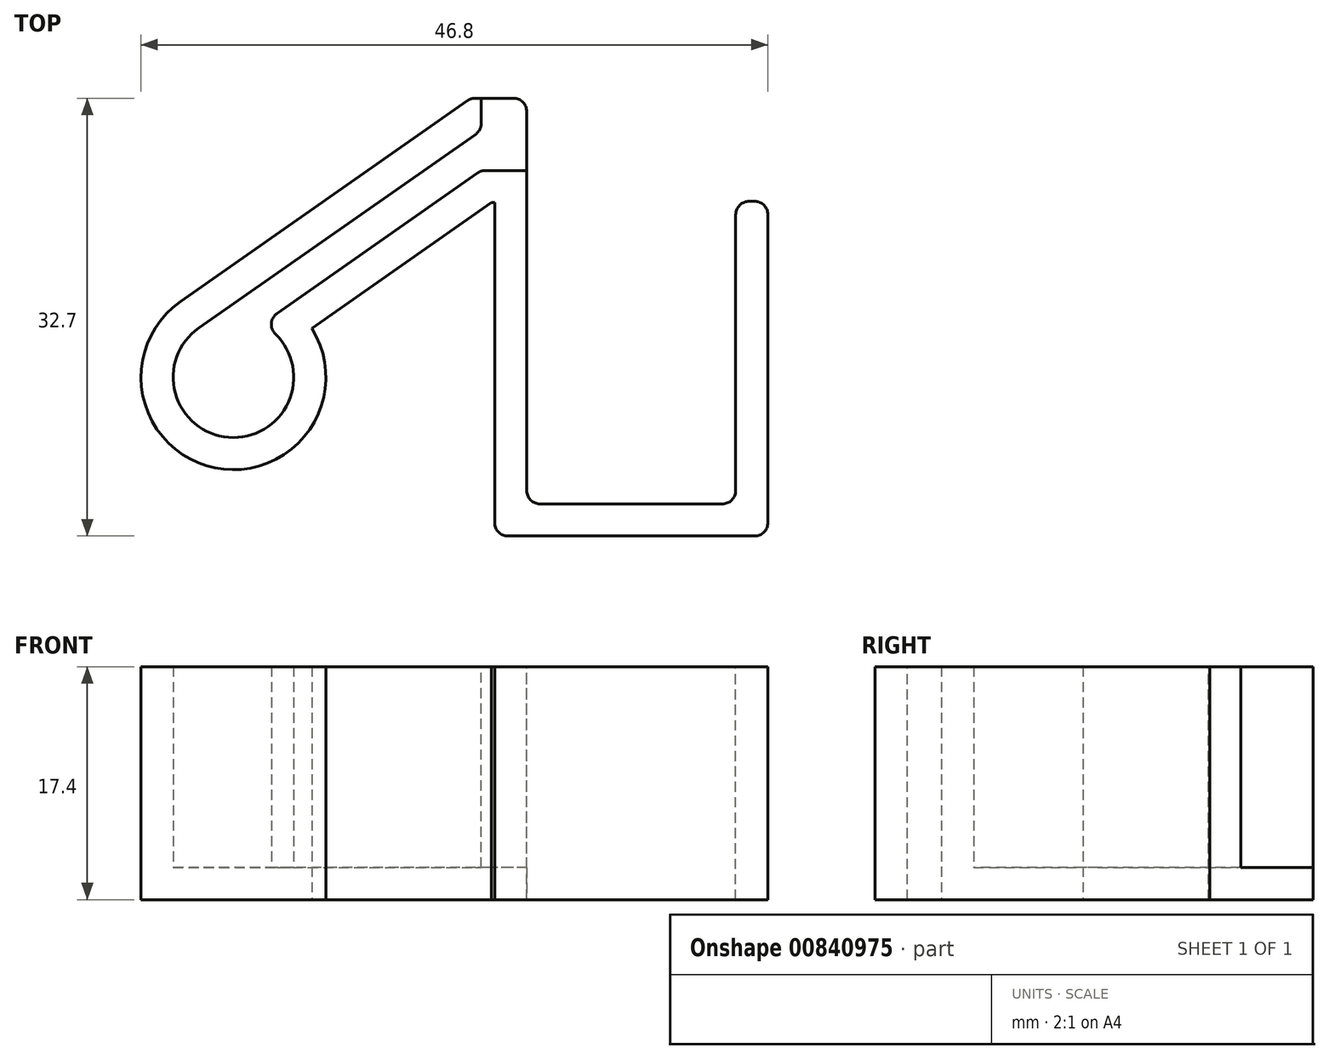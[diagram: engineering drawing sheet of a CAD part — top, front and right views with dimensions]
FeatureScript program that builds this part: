
annotation { "Feature Type Name" : "Feature", "Feature Type Description" : "" }
export const myFeature = defineFeature(function(context is Context, id is Id, definition is map)
    precondition{}
    {
        {
            var Q0;
            Q0=qCreatedBy(makeId("Top.planeOp"),FACE);
            var sketch = newSketch(context, id + "F0", { "sketchPlane" : qUnion([Q0])});
            skLineSegment(sketch, "E0.bottom", {"start": v(0, 0) * mm, "end": v(-1, 0) * mm});
            skLineSegment(sketch, "E0.top", {"start": v(0, 3) * mm, "end": v(-1, 3) * mm});
            skLineSegment(sketch, "E0.left", {"start": v(0, 0) * mm, "end": v(0, 3) * mm});
            skLineSegment(sketch, "E0.right", {"start": v(-1, 0) * mm, "end": v(-1, 3) * mm});
            skLineSegment(sketch, "E1", {"start": v(-1, 3) * mm, "end": v(-22.08, -11.76) * mm});
            skLineSegment(sketch, "E2", {"start": v(-17.38, -11.47) * mm, "end": v(-1, 0) * mm});
            skPoint(sketch, "E3.third.point", {"position": v(-34.17, -22.62) * mm});
            skCircle(sketch, "E4", {"center": v(-19.5, -15.44) * mm, "radius": 4.5 * mm});
            skPoint(sketch, "E4.third.point", {"position": v(-19.43, -19.94) * mm});
            skSolve(sketch);
        }
        {
            var Q0;
            Q0=makeQuery(id+"F0.imprint","IMPRINT",FACE,{"disambiguationData":[TD([[makeQuery(id+"F0.imprint","IMPRINT",EDGE,{"derivedFrom":sQuery(id+"F0.wireOp",EDGE,"E0.right")}),1.0]])]});
            var Q1;
            Q1=makeQuery(id+"F0.imprint","IMPRINT",FACE,{"disambiguationData":[TD([[makeQuery(id+"F0.imprint","IMPRINT",EDGE,{"derivedFrom":sQuery(id+"F0.wireOp",EDGE,"E0.bottom")}),-1.0]])]});
            var Q2;
            {var subQ0=sQuery(id+"F0.wireOp",EDGE,"E4");var subQ1=makeQuery(id+"F0.imprint","INTERSECT",VERTEX,{"derivedFrom":[sQuery(id+"F0.wireOp",EDGE,"E1"),subQ0]});Q2=makeQuery(id+"F0.imprint","IMPRINT",FACE,{"disambiguationData":[TD([[makeQuery(id+"F0.imprint","IMPRINT",EDGE,{"disambiguationData":[TD([[subQ1,1.0]])],"derivedFrom":subQ0}),1.0]])]});}
            extrude(context, id + "F1", {"entities" : qUnion([Q0, Q1, Q2]), "depth" : 15 * mm, "offsetDistance" : 25 * mm});
        }
        {
            var Q0;
            Q0=makeQuery(id+"F1.opExtrude","CAP_FACE",FACE,{"disambiguationData":[OSD([sQuery(id+"F0.wireOp",EDGE,"E0.bottom"),sQuery(id+"F0.wireOp",EDGE,"E0.top"),sQuery(id+"F0.wireOp",EDGE,"E0.left"),sQuery(id+"F0.wireOp",EDGE,"E1"),sQuery(id+"F0.wireOp",EDGE,"E2"),sQuery(id+"F0.wireOp",EDGE,"E4")])],"isStart":false});
            shell(context, id + "F2", {"entities" : qUnion([Q0]), "thickness" : 2.4 * mm, "oppositeDirection" : true});
        }
        {
            var Q0;
            Q0=makeQuery(id+"F1.opExtrude","CAP_FACE",FACE,{"disambiguationData":[OSD([sQuery(id+"F0.wireOp",EDGE,"E0.bottom"),sQuery(id+"F0.wireOp",EDGE,"E0.top"),sQuery(id+"F0.wireOp",EDGE,"E0.left"),sQuery(id+"F0.wireOp",EDGE,"E1"),sQuery(id+"F0.wireOp",EDGE,"E2"),sQuery(id+"F0.wireOp",EDGE,"E4")])],"isStart":false});
            var sketch = newSketch(context, id + "F3", { "sketchPlane" : qUnion([Q0])});
            skLineSegment(sketch, "E5.bottom", {"start": v(0, 0) * mm, "end": v(2.4, 0) * mm});
            skLineSegment(sketch, "E5.top", {"start": v(0, 3) * mm, "end": v(2.4, 3) * mm});
            skLineSegment(sketch, "E5.left", {"start": v(0, 0) * mm, "end": v(0, 3) * mm});
            skLineSegment(sketch, "E5.right", {"start": v(2.4, 0) * mm, "end": v(2.4, 3) * mm});
            skLineSegment(sketch, "E6.bottom", {"start": v(-1, 3) * mm, "end": v(-1, 3) * mm});
            skLineSegment(sketch, "E6.top", {"start": v(-1, 5.4) * mm, "end": v(-1, 5.4) * mm});
            skLineSegment(sketch, "E6.left", {"start": v(-1, 3) * mm, "end": v(-1, 5.4) * mm});
            skLineSegment(sketch, "E6.right", {"start": v(-1, 3) * mm, "end": v(-1, 5.4) * mm});
            skSolve(sketch);
        }
        {
            var Q0;
            Q0=makeQuery(id+"F3.imprint","IMPRINT",FACE,{"disambiguationData":[TD([[makeQuery(id+"F3.imprint","IMPRINT",EDGE,{"derivedFrom":sQuery(id+"F3.wireOp",EDGE,"E5.bottom")}),1.0]])]});
            var Q1;
            {var subQ5=sQuery(id+"F3.wireOp",EDGE,"E5.top");Q1=makeQuery(id+"F3.imprint","IMPRINT",FACE,{"disambiguationData":[TD([[makeQuery(id+"F3.imprint","IMPRINT",EDGE,{"derivedFrom":subQ5}),1.0]])]});}
            extrude(context, id + "F4", {"entities" : qUnion([Q0, Q1]), "operationType" : NewBodyOperationType.REMOVE, "oppositeDirection" : true, "depth" : 15 * mm, "offsetDistance" : 25 * mm});
        }
        {
            var Q0;
            Q0=makeQuery(id+"F2.opShell","OFFSET_EDGE",EDGE,{"disambiguationData":[OSD([sQuery(id+"F0.wireOp",EDGE,"E2"),sQuery(id+"F0.wireOp",EDGE,"E4")])]});
            var Q1;
            Q1=makeQuery(id+"F2.opShell","OFFSET_EDGE",EDGE,{"disambiguationData":[OSD([sQuery(id+"F0.wireOp",EDGE,"E0.bottom"),sQuery(id+"F0.wireOp",EDGE,"E0.right"),sQuery(id+"F0.wireOp",EDGE,"E2")])]});
            var Q2;
            Q2=makeQuery(id+"F2.opShell","OFFSET_EDGE",EDGE,{"disambiguationData":[OSD([sQuery(id+"F0.wireOp",EDGE,"E0.top"),sQuery(id+"F0.wireOp",EDGE,"E0.right"),sQuery(id+"F0.wireOp",EDGE,"E1")])]});
            var Q3;
            Q3=makeQuery(id+"F1.opExtrude","SWEPT_EDGE",EDGE,{"disambiguationData":[OSD([sQuery(id+"F0.wireOp",EDGE,"E0.top"),sQuery(id+"F0.wireOp",EDGE,"E0.right"),sQuery(id+"F0.wireOp",EDGE,"E1")])]});
            fillet(context, id + "F5", {"entities" : qUnion([Q0, Q1, Q2, Q3]), "radius" : 1 * mm, "tangentPropagation" : true, "defaultsChanged" : false, "vertexSettings" : [], "allowEdgeOverflow" : false});
        }
        {
            var Q0;
            Q0=qCreatedBy(makeId("Top.planeOp"),FACE);
            var sketch = newSketch(context, id + "F6", { "sketchPlane" : qUnion([Q0])});
            skLineSegment(sketch, "E7.bottom", {"start": v(0, 0) * mm, "end": v(2.4, 0) * mm, "construction": true});
            skLineSegment(sketch, "E7.top", {"start": v(0, -2.4) * mm, "end": v(2.4, -2.4) * mm, "construction": true});
            skLineSegment(sketch, "E7.left", {"start": v(0, 0) * mm, "end": v(0, -2.4) * mm, "construction": true});
            skLineSegment(sketch, "E7.right", {"start": v(2.4, 0) * mm, "end": v(2.4, -2.4) * mm, "construction": true});
            skLineSegment(sketch, "E8.bottom", {"start": v(0, -2.4) * mm, "end": v(2.4, -2.4) * mm});
            skLineSegment(sketch, "E8.top", {"start": v(0, -24.9) * mm, "end": v(2.4, -24.9) * mm});
            skLineSegment(sketch, "E8.left", {"start": v(0, -2.4) * mm, "end": v(0, -24.9) * mm});
            skLineSegment(sketch, "E8.right", {"start": v(2.4, -2.4) * mm, "end": v(2.4, -24.9) * mm});
            skLineSegment(sketch, "E9.bottom", {"start": v(0, -24.9) * mm, "end": v(18, -24.9) * mm});
            skLineSegment(sketch, "E9.top", {"start": v(0, -27.3) * mm, "end": v(18, -27.3) * mm});
            skLineSegment(sketch, "E9.left", {"start": v(0, -24.9) * mm, "end": v(0, -27.3) * mm});
            skLineSegment(sketch, "E9.right", {"start": v(18, -24.9) * mm, "end": v(18, -27.3) * mm});
            skLineSegment(sketch, "E10.bottom", {"start": v(18, -27.3) * mm, "end": v(20.4, -27.3) * mm});
            skLineSegment(sketch, "E10.top", {"start": v(18, -2.3) * mm, "end": v(20.4, -2.3) * mm});
            skLineSegment(sketch, "E10.left", {"start": v(18, -27.3) * mm, "end": v(18, -2.3) * mm});
            skLineSegment(sketch, "E10.right", {"start": v(20.4, -27.3) * mm, "end": v(20.4, -2.3) * mm});
            skSolve(sketch);
        }
        {
            var Q0;
            Q0=qSketchRegion(id+"F6",true);
            extrude(context, id + "F7", {"entities" : qUnion([Q0]), "operationType" : NewBodyOperationType.ADD, "oppositeDirection" : true, "depth" : 2.4 * mm, "offsetDistance" : 25 * mm});
        }
        {
            var Q0;
            Q0=makeQuery(id+"F6.imprint","IMPRINT",FACE,{"disambiguationData":[TD([[makeQuery(id+"F6.imprint","IMPRINT",EDGE,{"derivedFrom":sQuery(id+"F6.wireOp",EDGE,"E8.bottom")}),-1.0]])]});
            var Q1;
            {var subQ1=sQuery(id+"F6.wireOp",EDGE,"E9.top");Q1=makeQuery(id+"F6.imprint","IMPRINT",FACE,{"disambiguationData":[TD([[makeQuery(id+"F6.imprint","IMPRINT",EDGE,{"derivedFrom":subQ1}),1.0]])]});}
            var Q2;
            {var subQ3=sQuery(id+"F6.wireOp",EDGE,"E10.bottom");Q2=makeQuery(id+"F6.imprint","IMPRINT",FACE,{"disambiguationData":[TD([[makeQuery(id+"F6.imprint","IMPRINT",EDGE,{"derivedFrom":subQ3}),1.0]])]});}
            extrude(context, id + "F8", {"entities" : qUnion([Q0, Q1, Q2]), "operationType" : NewBodyOperationType.ADD, "depth" : 15 * mm, "offsetDistance" : 25 * mm});
        }
        {
            var Q0;
            {var subQ0=sQuery(id+"F6.wireOp",EDGE,"E10.left");var subQ1=sQuery(id+"F6.wireOp",EDGE,"E10.top");Q0=makeQuery(id+"F8.boolean.opBoolean","MERGE",EDGE,{"derivedFrom":[makeQuery(id+"F7.opExtrude","SWEPT_EDGE",EDGE,{"disambiguationData":[OSD([subQ1,subQ0])]}),makeQuery(id+"F8.opExtrude","SWEPT_EDGE",EDGE,{"disambiguationData":[OSD([subQ1,subQ0])]})]});}
            var Q1;
            {var subQ0=sQuery(id+"F6.wireOp",EDGE,"E10.right");var subQ1=sQuery(id+"F6.wireOp",EDGE,"E10.top");Q1=makeQuery(id+"F8.boolean.opBoolean","MERGE",EDGE,{"derivedFrom":[makeQuery(id+"F7.opExtrude","SWEPT_EDGE",EDGE,{"disambiguationData":[OSD([subQ1,subQ0])]}),makeQuery(id+"F8.opExtrude","SWEPT_EDGE",EDGE,{"disambiguationData":[OSD([subQ1,subQ0])]})]});}
            var Q2;
            {var subQ0=sQuery(id+"F6.wireOp",EDGE,"E10.right");var subQ1=sQuery(id+"F6.wireOp",EDGE,"E10.bottom");Q2=makeQuery(id+"F8.boolean.opBoolean","MERGE",EDGE,{"derivedFrom":[makeQuery(id+"F7.opExtrude","SWEPT_EDGE",EDGE,{"disambiguationData":[OSD([subQ1,subQ0])]}),makeQuery(id+"F8.opExtrude","SWEPT_EDGE",EDGE,{"disambiguationData":[OSD([subQ1,subQ0])]})]});}
            var Q3;
            {var subQ0=sQuery(id+"F6.wireOp",EDGE,"E10.left");var subQ1=sQuery(id+"F6.wireOp",EDGE,"E9.bottom");Q3=makeQuery(id+"F8.boolean.opBoolean","MERGE",EDGE,{"derivedFrom":[makeQuery(id+"F7.opExtrude","SWEPT_EDGE",EDGE,{"disambiguationData":[OSD([subQ1,subQ0])]}),makeQuery(id+"F8.opExtrude","SWEPT_EDGE",EDGE,{"disambiguationData":[OSD([subQ1,subQ0])]})]});}
            var Q4;
            {var subQ0=sQuery(id+"F6.wireOp",EDGE,"E9.left");var subQ1=sQuery(id+"F6.wireOp",EDGE,"E9.top");Q4=makeQuery(id+"F8.boolean.opBoolean","MERGE",EDGE,{"derivedFrom":[makeQuery(id+"F7.opExtrude","SWEPT_EDGE",EDGE,{"disambiguationData":[OSD([subQ1,subQ0])]}),makeQuery(id+"F8.opExtrude","SWEPT_EDGE",EDGE,{"disambiguationData":[OSD([subQ1,subQ0])]})]});}
            var Q5;
            {var subQ0=sQuery(id+"F6.wireOp",EDGE,"E9.bottom");var subQ1=sQuery(id+"F6.wireOp",EDGE,"E8.right");Q5=makeQuery(id+"F8.boolean.opBoolean","MERGE",EDGE,{"derivedFrom":[makeQuery(id+"F7.opExtrude","SWEPT_EDGE",EDGE,{"disambiguationData":[OSD([subQ1,subQ0])]}),makeQuery(id+"F8.opExtrude","SWEPT_EDGE",EDGE,{"disambiguationData":[OSD([subQ1,subQ0])]})]});}
            var Q6;
            {var subQ0=sQuery(id+"F6.wireOp",EDGE,"E8.left");var subQ1=sQuery(id+"F6.wireOp",EDGE,"E8.bottom");Q6=makeQuery(id+"F8.boolean.opBoolean","MERGE",EDGE,{"derivedFrom":[makeQuery(id+"F7.opExtrude","SWEPT_EDGE",EDGE,{"disambiguationData":[OSD([subQ1,subQ0])]}),makeQuery(id+"F8.opExtrude","SWEPT_EDGE",EDGE,{"disambiguationData":[OSD([subQ1,subQ0])]})]});}
            var Q7;
            Q7=makeQuery(id+"F4.boolean.opBoolean","COPY",EDGE,{"derivedFrom":makeQuery(id+"F4.opExtrude","SWEPT_EDGE",EDGE,{"disambiguationData":[OSD([sQuery(id+"F0.wireOp",EDGE,"E0.left"),sQuery(id+"F3.wireOp",EDGE,"E5.bottom"),sQuery(id+"F3.wireOp",EDGE,"E5.right")])]})});
            var Q8;
            Q8=makeQuery(id+"F1.opExtrude","SWEPT_EDGE",EDGE,{"disambiguationData":[OSD([sQuery(id+"F0.wireOp",EDGE,"E0.top"),sQuery(id+"F0.wireOp",EDGE,"E0.left")])]});
            fillet(context, id + "F9", {"entities" : qUnion([Q0, Q1, Q2, Q3, Q4, Q5, Q6, Q7, Q8]), "radius" : 1 * mm, "tangentPropagation" : true, "allowEdgeOverflow" : false});
        }
    });
